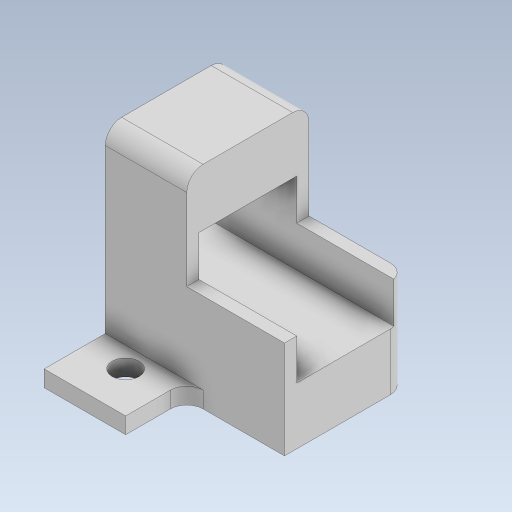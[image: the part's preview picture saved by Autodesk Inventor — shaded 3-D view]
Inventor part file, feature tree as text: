
AUTODESK INVENTOR PART (.ipt)
format: ipt  version: 2023.5 (Build 275446000, 446)  size: 163,840 bytes
history: native  units: mm
features: extrude x4, sketch x2, fillet x1
ambient origin geometry x8: Origin, YZ Plane, XZ Plane, XY Plane, X Axis, Y Axis, Z Axis, Center Point
bodies: Solid1 (feature_tree)
feature tree (7):
  sketch  "Sketch1"  dims[d3=3.3mm d6=3.3mm]
  extrude  "Extrusion1"  Depth=3.3mm
  extrude  "Extrusion2"  Depth=24.0mm TaperAngle=0.0deg
  sketch  "Sketch2"  dims[d9=2.0mm d10=0.0mm d11=24.0mm d12=0.0mm d13=7.0mm d14=10.0mm d15=24.0mm d16=0.0mm d17=12.0mm d18=0.0mm d19=2.0mm d20=0.5mm d21=0.872665mm d22=0.5mm d23=0.872665mm]
  extrude  "Extrusion3"  Depth=7.0mm
  extrude  "Extrusion4"  Depth=10.0mm
  fillet  "Fillet1"  Radius=24.0mm
